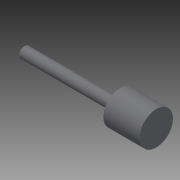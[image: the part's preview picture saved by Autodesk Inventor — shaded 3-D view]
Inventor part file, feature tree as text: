
AUTODESK INVENTOR PART (.ipt)
format: ipt  version: 2014 (Build 180170000, 170)  size: 118,784 bytes
history: native  units: in
note: dims shown in document units (in); Inventor stores cm internally (conversion verified against a paired STEP export)
features: other x49, revolve x2, sketch x2
ambient origin geometry x8: Origin, YZ Plane, XZ Plane, XY Plane, X Axis, Y Axis, Z Axis, Center Point
bodies: Solid1 (feature_tree)
feature tree (53):
  revolve  "Revolution1"  Angle=360.0deg
  revolve  "Revolution2"  [1 undecoded]
  other  "h1_XY"
  other  "h1_YZ"
  other  "h1_ZX"
  other  "h1_X"
  other  "h1_Y"
  other  "h1_Z"
  other  "h1_Center"
  other  "h2_XY"
  other  "h2_YZ"
  other  "h2_ZX"
  other  "h2_X"
  other  "h2_Y"
  other  "h2_Z"
  other  "h2_Center"
  other  "k1_XY"
  other  "k1_YZ"
  other  "k1_ZX"
  other  "k1_X"
  other  "k1_Y"
  other  "k1_Z"
  other  "k1_Center"
  other  "k2_XY"
  other  "k2_YZ"
  other  "k2_ZX"
  other  "k2_X"
  other  "k2_Y"
  other  "k2_Z"
  other  "k2_Center"
  other  "start_XY"
  other  "start_YZ"
  other  "start_ZX"
  other  "start_X"
  other  "start_Y"
  other  "start_Z"
  other  "start_Center"
  other  "to_prc_XY"
  other  "to_prc_YZ"
  other  "to_prc_ZX"
  other  "to_prc_X"
  other  "to_prc_Y"
  other  "to_prc_Z"
  other  "to_prc_Center"
  other  "to_rod_guide_XY"
  other  "to_rod_guide_YZ"
  other  "to_rod_guide_ZX"
  other  "to_rod_guide_X"
  other  "to_rod_guide_Y"
  other  "to_rod_guide_Z"
  other  "to_rod_guide_Center"
  sketch  "Sketch_5"  dims[d0=360.0deg d1=360.0deg]
  sketch  "Sketch_14"
note: 1 required parameter value undecoded (feature->parameter linkage not recoverable at this tier; creation-order binding heuristic only, values carry confidence <= 0.55)
